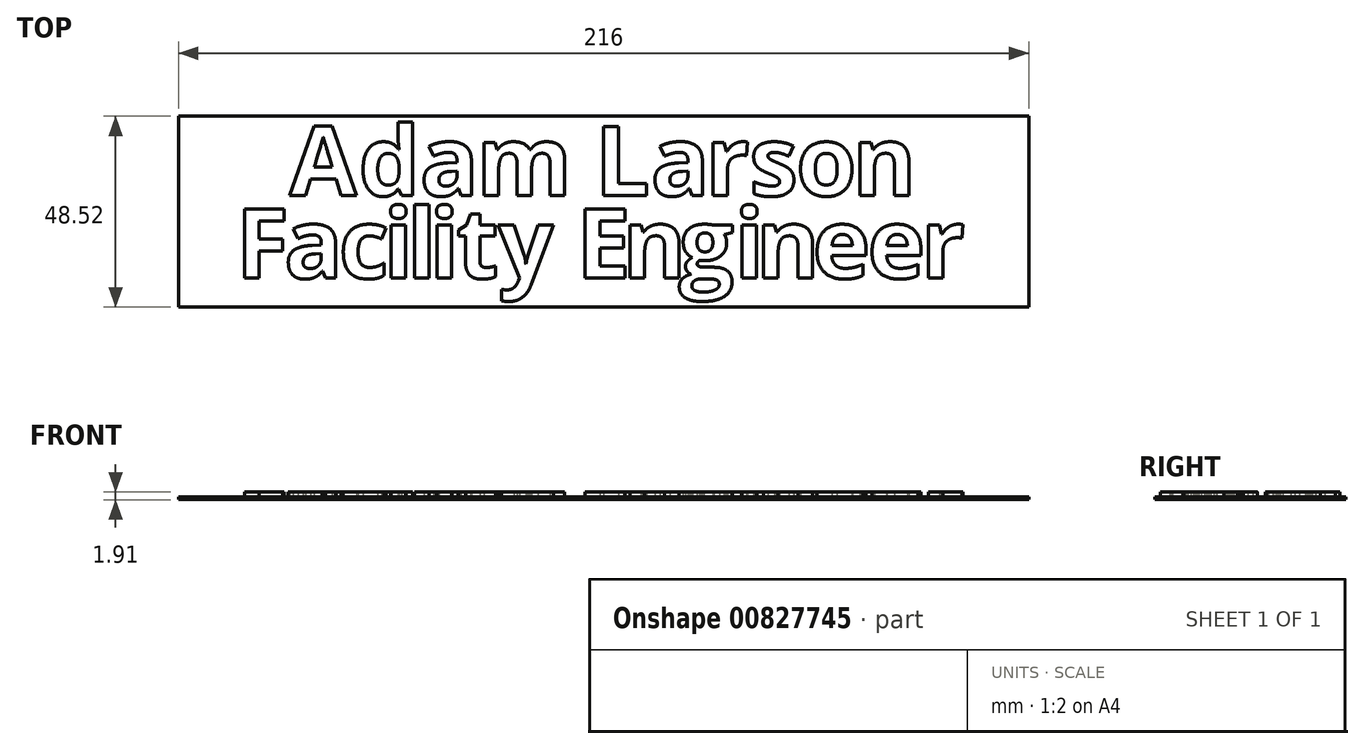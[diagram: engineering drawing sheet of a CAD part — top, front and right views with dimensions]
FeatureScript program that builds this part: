
annotation { "Feature Type Name" : "Feature", "Feature Type Description" : "" }
export const myFeature = defineFeature(function(context is Context, id is Id, definition is map)
    precondition{}
    {
        {
            var Q0;
            Q0=qCreatedBy(makeId("Top.planeOp"),FACE);
            var sketch = newSketch(context, id + "F0", { "sketchPlane" : qUnion([Q0])});
            skText(sketch, "E0", { "text": "A", "fontName": "OpenSans-Bold.ttf"});
            skText(sketch, "E1", { "text": "d", "fontName": "OpenSans-Bold.ttf"});
            skText(sketch, "E2", { "text": "a", "fontName": "OpenSans-Bold.ttf"});
            skText(sketch, "E3", { "text": "m", "fontName": "OpenSans-Bold.ttf"});
            skText(sketch, "E4", { "text": "L", "fontName": "OpenSans-Bold.ttf"});
            skText(sketch, "E5", { "text": "a", "fontName": "OpenSans-Bold.ttf"});
            skText(sketch, "E6", { "text": "r", "fontName": "OpenSans-Bold.ttf"});
            skText(sketch, "E7", { "text": "s", "fontName": "OpenSans-Bold.ttf"});
            skText(sketch, "E8", { "text": "o", "fontName": "OpenSans-Bold.ttf"});
            skText(sketch, "E9", { "text": "F", "fontName": "OpenSans-Bold.ttf"});
            skText(sketch, "E10", { "text": "a", "fontName": "OpenSans-Bold.ttf"});
            skText(sketch, "E11", { "text": "c", "fontName": "OpenSans-Bold.ttf"});
            skText(sketch, "E12", { "text": "i", "fontName": "OpenSans-Bold.ttf"});
            skText(sketch, "E13", { "text": "l", "fontName": "OpenSans-Bold.ttf"});
            skText(sketch, "E14", { "text": "i", "fontName": "OpenSans-Bold.ttf"});
            skText(sketch, "E15", { "text": "t", "fontName": "OpenSans-Bold.ttf"});
            skText(sketch, "E16", { "text": "y", "fontName": "OpenSans-Bold.ttf"});
            skLineSegment(sketch, "E17", {"start": v(-68.52, 7.21) * mm, "end": v(4.66, 7.21) * mm});
            skLineSegment(sketch, "E18", {"start": v(25.7, -38.5) * mm, "end": v(-69.35, -38.5) * mm});
            skText(sketch, "E19", { "text": "n", "fontName": "OpenSans-Bold.ttf"});
            skText(sketch, "E20", { "text": "E", "fontName": "OpenSans-Bold.ttf"});
            skText(sketch, "E21", { "text": "n", "fontName": "OpenSans-Bold.ttf"});
            skText(sketch, "E22", { "text": "g", "fontName": "OpenSans-Bold.ttf"});
            skText(sketch, "E23", { "text": "i", "fontName": "OpenSans-Bold.ttf"});
            skText(sketch, "E24", { "text": "n", "fontName": "OpenSans-Bold.ttf"});
            skText(sketch, "E25", { "text": "e", "fontName": "OpenSans-Bold.ttf"});
            skText(sketch, "E26", { "text": "e", "fontName": "OpenSans-Bold.ttf"});
            skText(sketch, "E27", { "text": "r", "fontName": "OpenSans-Bold.ttf"});
            const initialGuessF0  = {"E0": [-0.03354, -0.01158, 1, 0, 0.01778], "E1": [-0.016, -0.01158, 1, 0, 0.01778], "E2": [-0.00043, -0.01158, 1, 0, 0.01778], "E3": [0.01395, -0.01158, 1, 0, 0.01778], "E4": [0.044, -0.01158, 1, 0, 0.01778], "E5": [0.05824, -0.01158, 1, 0, 0.01778], "E6": [0.07212, -0.01158, 1, 0, 0.01778], "E7": [0.08323, -0.01158, 1, 0, 0.01778], "E8": [0.09515, -0.01158, 1, 0, 0.01778], "E9": [-0.04725, -0.03254, 1, 0, 0.01778], "E10": [-0.03492, -0.03254, 1, 0, 0.01778], "E11": [-0.02102, -0.03254, 1, 0, 0.01778], "E12": [-0.00969, -0.03254, 1, 0, 0.01778], "E13": [-0.00376, -0.03254, 1, 0, 0.01778], "E14": [0.002, -0.03254, 1, 0, 0.01778], "E15": [0.00881, -0.03254, 1, 0, 0.01778], "E16": [0.01945, -0.03254, 1, 0, 0.01778], "E19": [0.1094, -0.01158, 1, 0, 0.01778], "E20": [0.03934, -0.03254, 1, 0, 0.01778], "E21": [0.05104, -0.03254, 1, 0, 0.01778], "E22": [0.06536, -0.03254, 1, 0, 0.01778], "E23": [0.07947, -0.03254, 1, 0, 0.01778], "E24": [0.08495, -0.03254, 1, 0, 0.01778], "E25": [0.09934, -0.03254, 1, 0, 0.01778], "E26": [0.1133, -0.03254, 1, 0, 0.01778], "E27": [0.1268, -0.03254, 1, 0, 0.01778]};
            skSetInitialGuess(sketch, initialGuessF0);
            skSolve(sketch);
        }
        {
            var Q0;
            Q0 = qSketchRegion(id + "F0", true);
            extrude(context, id + "F1", {"entities" : qUnion([Q0]), "depth" : 1.27 * mm, "offsetDistance" : 25.4 * mm});
        }
        {
            var Q0;
            Q0=qCreatedBy(makeId("Top.planeOp"),FACE);
            var sketch = newSketch(context, id + "F2", { "sketchPlane" : qUnion([Q0])});
            skLineSegment(sketch, "E28.bottom", {"start": v(-61.77, 8.62) * mm, "end": v(154.23, 8.62) * mm});
            skLineSegment(sketch, "E28.top", {"start": v(-61.77, -39.9) * mm, "end": v(154.23, -39.9) * mm});
            skLineSegment(sketch, "E28.left", {"start": v(-61.77, 8.62) * mm, "end": v(-61.77, -39.9) * mm});
            skLineSegment(sketch, "E28.right", {"start": v(154.23, 8.62) * mm, "end": v(154.23, -39.9) * mm});
            skLineSegment(sketch, "E29.0", {"start": v(-5.98, 7.18) * mm, "end": v(-2.29, 7.18) * mm});
            skPoint(sketch, "E30.0", {"position": v(71.24, -38.47) * mm});
            skPoint(sketch, "E31.0", {"position": v(22.16, -38.47) * mm});
            skLineSegment(sketch, "E32.0", {"start": v(-45.03, -32.54) * mm, "end": v(-45.03, -14.9) * mm});
            skPoint(sketch, "E33.0", {"position": v(137.49, -18.91) * mm});
            skSolve(sketch);
        }
        {
            var Q0;
            Q0=makeQuery(id+"F2.imprint","IMPRINT",FACE,{"disambiguationData":[TD([[makeQuery(id+"F2.imprint","IMPRINT",EDGE,{"derivedFrom":sQuery(id+"F2.wireOp",EDGE,"E28.bottom")}),-1.0]])]});
            extrude(context, id + "F3", {"entities" : qUnion([Q0]), "operationType" : NewBodyOperationType.ADD, "oppositeDirection" : true, "depth" : 0.64 * mm, "offsetDistance" : 25.4 * mm});
        }
    });
